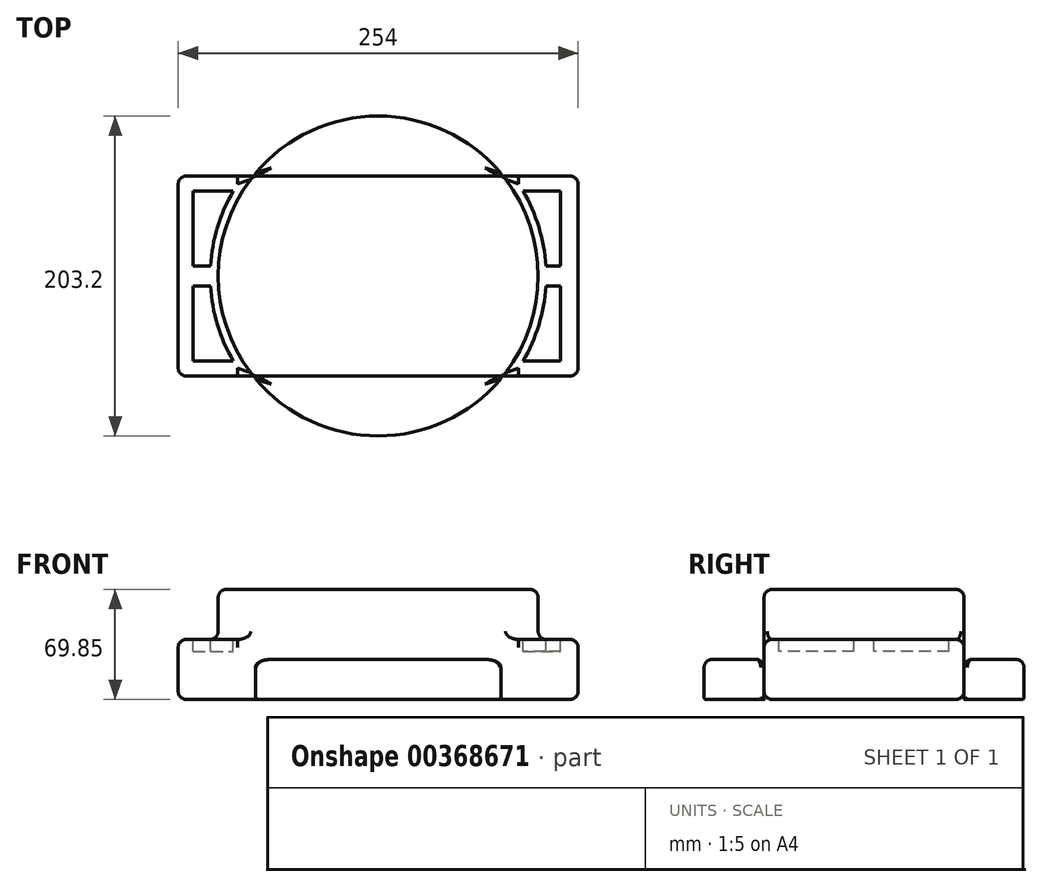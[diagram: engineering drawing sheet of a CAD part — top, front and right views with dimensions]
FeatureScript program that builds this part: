
annotation { "Feature Type Name" : "Feature", "Feature Type Description" : "" }
export const myFeature = defineFeature(function(context is Context, id is Id, definition is map)
    precondition{}
    {
        {
            var Q0;
            Q0=qCreatedBy(makeId("Top.planeOp"),FACE);
            var sketch = newSketch(context, id + "F0", { "sketchPlane" : qUnion([Q0])});
            skLineSegment(sketch, "E0.bottom", {"start": v(-127, 63.5) * mm, "end": v(127, 63.5) * mm});
            skLineSegment(sketch, "E0.top", {"start": v(-127, -63.5) * mm, "end": v(127, -63.5) * mm});
            skLineSegment(sketch, "E0.left", {"start": v(-127, 63.5) * mm, "end": v(-127, -63.5) * mm});
            skLineSegment(sketch, "E0.right", {"start": v(127, 63.5) * mm, "end": v(127, -63.5) * mm});
            skLineSegment(sketch, "E1", {"start": v(0, 63.5) * mm, "end": v(0, -63.5) * mm, "construction": true});
            skLineSegment(sketch, "E2", {"start": v(-127, 0) * mm, "end": v(127, 0) * mm, "construction": true});
            skPoint(sketch, "E3", {"position": v(0, 0) * mm});
            skCircle(sketch, "E4", {"center": v(0, 0) * mm, "radius": 101.6 * mm});
            skLineSegment(sketch, "E5", {"start": v(0, 63.5) * mm, "end": v(0, 101.6) * mm});
            skLineSegment(sketch, "E6", {"start": v(0, -63.5) * mm, "end": v(0, -101.6) * mm});
            skSolve(sketch);
        }
        {
            var Q0;
            {var subQ0=sQuery(id+"F0.wireOp",EDGE,"E5");Q0=makeQuery(id+"F0.imprint","IMPRINT",FACE,{"disambiguationData":[TD([[makeQuery(id+"F0.imprint","IMPRINT",EDGE,{"derivedFrom":subQ0}),-1.0]])]});}
            var Q1;
            {var subQ0=sQuery(id+"F0.wireOp",EDGE,"E5");Q1=makeQuery(id+"F0.imprint","IMPRINT",FACE,{"disambiguationData":[TD([[makeQuery(id+"F0.imprint","IMPRINT",EDGE,{"derivedFrom":subQ0}),1.0]])]});}
            var Q2;
            {var subQ0=sQuery(id+"F0.wireOp",EDGE,"E6");Q2=makeQuery(id+"F0.imprint","IMPRINT",FACE,{"disambiguationData":[TD([[makeQuery(id+"F0.imprint","IMPRINT",EDGE,{"derivedFrom":subQ0}),-1.0]])]});}
            var Q3;
            {var subQ0=sQuery(id+"F0.wireOp",EDGE,"E6");Q3=makeQuery(id+"F0.imprint","IMPRINT",FACE,{"disambiguationData":[TD([[makeQuery(id+"F0.imprint","IMPRINT",EDGE,{"derivedFrom":subQ0}),1.0]])]});}
            extrude(context, id + "F1", {"entities" : qUnion([Q0, Q1, Q2, Q3]), "depth" : 25.4 * mm});
        }
        {
            var Q0;
            Q0=makeQuery(id+"FdMcATzVPKO9tzP_2.opExtrude","CAP_FACE",FACE,{"disambiguationData":[OSD([sQuery(id+"F0.wireOp",EDGE,"E0.bottom"),sQuery(id+"F0.wireOp",EDGE,"E0.top"),sQuery(id+"F0.wireOp",EDGE,"E0.left"),sQuery(id+"F0.wireOp",EDGE,"E0.right")])],"isStart":false});
            var Q1;
            Q1=makeQuery(id+"FdMcATzVPKO9tzP_2.opExtrude","SWEPT_FACE",FACE,{"disambiguationData":[OSD([sQuery(id+"F0.wireOp",EDGE,"E0.top")])]});
            var Q2;
            Q2=makeQuery(id+"FdMcATzVPKO9tzP_2.opExtrude","SWEPT_FACE",FACE,{"disambiguationData":[OSD([sQuery(id+"F0.wireOp",EDGE,"E0.left")])]});
            var Q3;
            Q3=makeQuery(id+"FdMcATzVPKO9tzP_2.opExtrude","SWEPT_FACE",FACE,{"disambiguationData":[OSD([sQuery(id+"F0.wireOp",EDGE,"E0.right")])]});
            var Q4;
            Q4=makeQuery(id+"FdMcATzVPKO9tzP_2.opExtrude","SWEPT_FACE",FACE,{"disambiguationData":[OSD([sQuery(id+"F0.wireOp",EDGE,"E0.bottom")])]});
            var Q5;
            Q5=makeQuery(id+"F1.opExtrude","CAP_FACE",FACE,{"disambiguationData":[OSD([sQuery(id+"F0.wireOp",EDGE,"E0.top"),sQuery(id+"F0.wireOp",EDGE,"E4")])],"isStart":false});
            var Q6;
            Q6=makeQuery(id+"F1.opExtrude","CAP_FACE",FACE,{"disambiguationData":[OSD([sQuery(id+"F0.wireOp",EDGE,"E0.bottom"),sQuery(id+"F0.wireOp",EDGE,"E4")])],"isStart":false});
            fillet(context, id + "F2", {"entities" : qUnion([Q0, Q1, Q2, Q3, Q4, Q5, Q6]), "radius" : 5.08 * mm, "tangentPropagation" : true, "allowEdgeOverflow" : false});
        }
        {
            var Q0;
            {var subQ0=sQuery(id+"F0.wireOp",EDGE,"E4");var subQ1=makeQuery(id+"F0.imprint","INTERSECT",VERTEX,{"derivedFrom":[subQ0,sQuery(id+"F0.wireOp",EDGE,"E5")]});Q0=makeQuery(id+"F1.opExtrude","SWEPT_FACE",FACE,{"disambiguationData":[OSD([subQ0]),TDD([makeQuery(id+"F0.imprint","IMPRINT",EDGE,{"disambiguationData":[TD([[subQ1,1.0]])],"derivedFrom":subQ0}),makeQuery(id+"F0.imprint","IMPRINT",EDGE,{"disambiguationData":[TD([[subQ1,-1.0]])],"derivedFrom":subQ0})])]});}
            var Q1;
            {var subQ0=sQuery(id+"F0.wireOp",EDGE,"E4");var subQ1=makeQuery(id+"F0.imprint","INTERSECT",VERTEX,{"derivedFrom":[subQ0,sQuery(id+"F0.wireOp",EDGE,"E6")]});Q1=makeQuery(id+"F1.opExtrude","SWEPT_FACE",FACE,{"disambiguationData":[OSD([subQ0]),TDD([makeQuery(id+"F0.imprint","IMPRINT",EDGE,{"disambiguationData":[TD([[subQ1,1.0]])],"derivedFrom":subQ0}),makeQuery(id+"F0.imprint","IMPRINT",EDGE,{"disambiguationData":[TD([[subQ1,-1.0]])],"derivedFrom":subQ0})])]});}
            fillet(context, id + "F3", {"entities" : qUnion([Q0, Q1]), "radius" : 1.27 * mm, "tangentPropagation" : true, "allowEdgeOverflow" : false});
        }
        {
            var Q0;
            {var subQ4=sQuery(id+"F0.wireOp",EDGE,"E0.bottom");var subQ5=makeQuery(id+"F0.imprint","INTERSECT",VERTEX,{"derivedFrom":[subQ4,sQuery(id+"F0.wireOp",EDGE,"E5")]});Q0=makeQuery(id+"F0.imprint","IMPRINT",FACE,{"disambiguationData":[TD([[makeQuery(id+"F0.imprint","IMPRINT",EDGE,{"disambiguationData":[TD([[subQ5,1.0]])],"derivedFrom":subQ4}),-1.0]])]});}
            extrude(context, id + "F4", {"entities" : qUnion([Q0]), "depth" : 69.85 * mm});
        }
        {
            var Q0;
            Q0=makeQuery(id+"F4.opExtrude","CAP_FACE",FACE,{"disambiguationData":[OSD([sQuery(id+"F0.wireOp",EDGE,"E0.bottom"),sQuery(id+"F0.wireOp",EDGE,"E0.top"),sQuery(id+"F0.wireOp",EDGE,"E4")])],"isStart":false});
            fillet(context, id + "F5", {"entities" : qUnion([Q0]), "radius" : 5.08 * mm, "tangentPropagation" : true, "allowEdgeOverflow" : false});
        }
        {
            var Q0;
            {var subQ0=sQuery(id+"F0.wireOp",EDGE,"E0.right");Q0=makeQuery(id+"F0.imprint","IMPRINT",FACE,{"disambiguationData":[TD([[makeQuery(id+"F0.imprint","IMPRINT",EDGE,{"derivedFrom":subQ0}),-1.0]])]});}
            var Q1;
            {var subQ0=sQuery(id+"F0.wireOp",EDGE,"E0.left");Q1=makeQuery(id+"F0.imprint","IMPRINT",FACE,{"disambiguationData":[TD([[makeQuery(id+"F0.imprint","IMPRINT",EDGE,{"derivedFrom":subQ0}),1.0]])]});}
            extrude(context, id + "F6", {"entities" : qUnion([Q0, Q1]), "operationType" : NewBodyOperationType.ADD, "depth" : 38.1 * mm});
        }
        {
            var Q0;
            Q0=makeQuery(id+"F6.opExtrude","CAP_FACE",FACE,{"disambiguationData":[OSD([sQuery(id+"F0.wireOp",EDGE,"E0.bottom"),sQuery(id+"F0.wireOp",EDGE,"E0.top"),sQuery(id+"F0.wireOp",EDGE,"E0.right"),sQuery(id+"F0.wireOp",EDGE,"E4")])],"isStart":false});
            var Q1;
            {var subQ0=sQuery(id+"F0.wireOp",EDGE,"E0.top");Q1=makeQuery(id+"F6.boolean.opBoolean","MERGE",FACE,{"derivedFrom":[makeQuery(id+"F4.opExtrude","SWEPT_FACE",FACE,{"disambiguationData":[OSD([subQ0])]}),makeQuery(id+"F6.opExtrude","SWEPT_FACE",FACE,{"disambiguationData":[OSD([subQ0]),TDD([makeQuery(id+"F0.imprint","IMPRINT",EDGE,{"disambiguationData":[TD([[makeQuery(id+"F0.imprint","INTERSECT",VERTEX,{"derivedFrom":[subQ0,sQuery(id+"F0.wireOp",EDGE,"E0.left")]}),-1.0]])],"derivedFrom":subQ0})])]}),makeQuery(id+"F6.opExtrude","SWEPT_FACE",FACE,{"disambiguationData":[OSD([subQ0]),TDD([makeQuery(id+"F0.imprint","IMPRINT",EDGE,{"disambiguationData":[TD([[makeQuery(id+"F0.imprint","INTERSECT",VERTEX,{"derivedFrom":[subQ0,sQuery(id+"F0.wireOp",EDGE,"E0.right")]}),1.0]])],"derivedFrom":subQ0})])]})]});}
            var Q2;
            Q2=makeQuery(id+"F6.opExtrude","SWEPT_FACE",FACE,{"disambiguationData":[OSD([sQuery(id+"F0.wireOp",EDGE,"E0.right")])]});
            var Q3;
            Q3=makeQuery(id+"F6.opExtrude","SWEPT_FACE",FACE,{"disambiguationData":[OSD([sQuery(id+"F0.wireOp",EDGE,"E0.left")])]});
            var Q4;
            Q4=makeQuery(id+"F6.opExtrude","CAP_FACE",FACE,{"disambiguationData":[OSD([sQuery(id+"F0.wireOp",EDGE,"E0.bottom"),sQuery(id+"F0.wireOp",EDGE,"E0.top"),sQuery(id+"F0.wireOp",EDGE,"E0.left"),sQuery(id+"F0.wireOp",EDGE,"E4")])],"isStart":false});
            var Q5;
            {var subQ0=sQuery(id+"F0.wireOp",EDGE,"E0.bottom");Q5=makeQuery(id+"F6.boolean.opBoolean","MERGE",FACE,{"derivedFrom":[makeQuery(id+"F4.opExtrude","SWEPT_FACE",FACE,{"disambiguationData":[OSD([subQ0])]}),makeQuery(id+"F6.opExtrude","SWEPT_FACE",FACE,{"disambiguationData":[OSD([subQ0]),TDD([makeQuery(id+"F0.imprint","IMPRINT",EDGE,{"disambiguationData":[TD([[makeQuery(id+"F0.imprint","INTERSECT",VERTEX,{"derivedFrom":[subQ0,sQuery(id+"F0.wireOp",EDGE,"E0.left")]}),-1.0]])],"derivedFrom":subQ0})])]}),makeQuery(id+"F6.opExtrude","SWEPT_FACE",FACE,{"disambiguationData":[OSD([subQ0]),TDD([makeQuery(id+"F0.imprint","IMPRINT",EDGE,{"disambiguationData":[TD([[makeQuery(id+"F0.imprint","INTERSECT",VERTEX,{"derivedFrom":[subQ0,sQuery(id+"F0.wireOp",EDGE,"E0.right")]}),1.0]])],"derivedFrom":subQ0})])]})]});}
            fillet(context, id + "F7", {"entities" : qUnion([Q0, Q1, Q2, Q3, Q4, Q5]), "radius" : 5.08 * mm, "tangentPropagation" : true, "allowEdgeOverflow" : false});
        }
        {
            var Q0;
            Q0=makeQuery(id+"F6.opExtrude","CAP_FACE",FACE,{"disambiguationData":[OSD([sQuery(id+"F0.wireOp",EDGE,"E0.bottom"),sQuery(id+"F0.wireOp",EDGE,"E0.top"),sQuery(id+"F0.wireOp",EDGE,"E0.left"),sQuery(id+"F0.wireOp",EDGE,"E4")])],"isStart":false});
            var sketch = newSketch(context, id + "F8", { "sketchPlane" : qUnion([Q0])});
            skLineSegment(sketch, "E7.bottom", {"start": v(-117.48, 53.98) * mm, "end": v(-92.02, 53.98) * mm});
            skLineSegment(sketch, "E7.top", {"start": v(-117.48, -53.98) * mm, "end": v(-92.02, -53.98) * mm});
            skLineSegment(sketch, "E7.left", {"start": v(-117.48, 53.98) * mm, "end": v(-117.48, -53.98) * mm});
            skLineSegment(sketch, "E7.right", {"start": v(-92.02, 53.98) * mm, "end": v(-92.02, -53.98) * mm});
            skArc(sketch, "E8", {"start": v(-92.02, 53.97) * mm, "mid": v(-106.66, 0) * mm, "end": v(-92.02, -53.97) * mm});
            skPoint(sketch, "E9", {"position": v(-117.48, 6.35) * mm});
            skPoint(sketch, "E10", {"position": v(-117.48, -6.35) * mm});
            skLineSegment(sketch, "E11", {"start": v(-117.48, 6.35) * mm, "end": v(-106.5, 6.35) * mm});
            skLineSegment(sketch, "E12", {"start": v(-117.48, -6.35) * mm, "end": v(-106.5, -6.35) * mm});
            skSolve(sketch);
        }
        {
            var Q0;
            {var subQ0=sQuery(id+"F8.wireOp",EDGE,"E7.bottom");Q0=makeQuery(id+"F8.imprint","IMPRINT",FACE,{"disambiguationData":[TD([[makeQuery(id+"F8.imprint","IMPRINT",EDGE,{"derivedFrom":subQ0}),-1.0]])]});}
            var Q1;
            {var subQ0=sQuery(id+"F8.wireOp",EDGE,"E7.top");Q1=makeQuery(id+"F8.imprint","IMPRINT",FACE,{"disambiguationData":[TD([[makeQuery(id+"F8.imprint","IMPRINT",EDGE,{"derivedFrom":subQ0}),1.0]])]});}
            extrude(context, id + "F9", {"entities" : qUnion([Q0, Q1]), "operationType" : NewBodyOperationType.REMOVE, "oppositeDirection" : true, "depth" : 7.62 * mm});
        }
        {
            var Q0;
            Q0=makeQuery(id+"F6.opExtrude","CAP_FACE",FACE,{"disambiguationData":[OSD([sQuery(id+"F0.wireOp",EDGE,"E0.bottom"),sQuery(id+"F0.wireOp",EDGE,"E0.top"),sQuery(id+"F0.wireOp",EDGE,"E0.right"),sQuery(id+"F0.wireOp",EDGE,"E4")])],"isStart":false});
            var sketch = newSketch(context, id + "F10", { "sketchPlane" : qUnion([Q0])});
            skLineSegment(sketch, "E13", {"start": v(115.94, 53.98) * mm, "end": v(115.94, -53.97) * mm});
            skArc(sketch, "E14", {"start": v(92.02, -53.97) * mm, "mid": v(106.68, 0) * mm, "end": v(92.02, 53.97) * mm});
            skLineSegment(sketch, "E15", {"start": v(92.02, -53.97) * mm, "end": v(115.94, -53.97) * mm});
            skLineSegment(sketch, "E16", {"start": v(92.02, 53.97) * mm, "end": v(115.94, 53.98) * mm});
            skPoint(sketch, "E17", {"position": v(115.94, 0) * mm});
            skLineSegment(sketch, "E18", {"start": v(0, 0) * mm, "end": v(162.81, 0) * mm, "construction": true});
            skPoint(sketch, "E18.endSnap0", {"position": v(121.92, 0) * mm});
            skPoint(sketch, "E19", {"position": v(115.94, 6.35) * mm});
            skPoint(sketch, "E20", {"position": v(115.94, -6.35) * mm});
            skPoint(sketch, "E21.endSnap0", {"position": v(106.68, 0) * mm});
            skLineSegment(sketch, "E22", {"start": v(115.94, -6.35) * mm, "end": v(106.5, -6.35) * mm});
            skLineSegment(sketch, "E23", {"start": v(115.94, 6.35) * mm, "end": v(106.5, 6.35) * mm});
            skSolve(sketch);
        }
        {
            var Q0;
            {var subQ0=sQuery(id+"F10.wireOp",EDGE,"E15");Q0=makeQuery(id+"F10.imprint","IMPRINT",FACE,{"disambiguationData":[TD([[makeQuery(id+"F10.imprint","IMPRINT",EDGE,{"derivedFrom":subQ0}),1.0]])]});}
            var Q1;
            {var subQ0=sQuery(id+"F10.wireOp",EDGE,"E16");Q1=makeQuery(id+"F10.imprint","IMPRINT",FACE,{"disambiguationData":[TD([[makeQuery(id+"F10.imprint","IMPRINT",EDGE,{"derivedFrom":subQ0}),-1.0]])]});}
            extrude(context, id + "F11", {"entities" : qUnion([Q0, Q1]), "operationType" : NewBodyOperationType.REMOVE, "oppositeDirection" : true, "depth" : 7.62 * mm});
        }
    });
